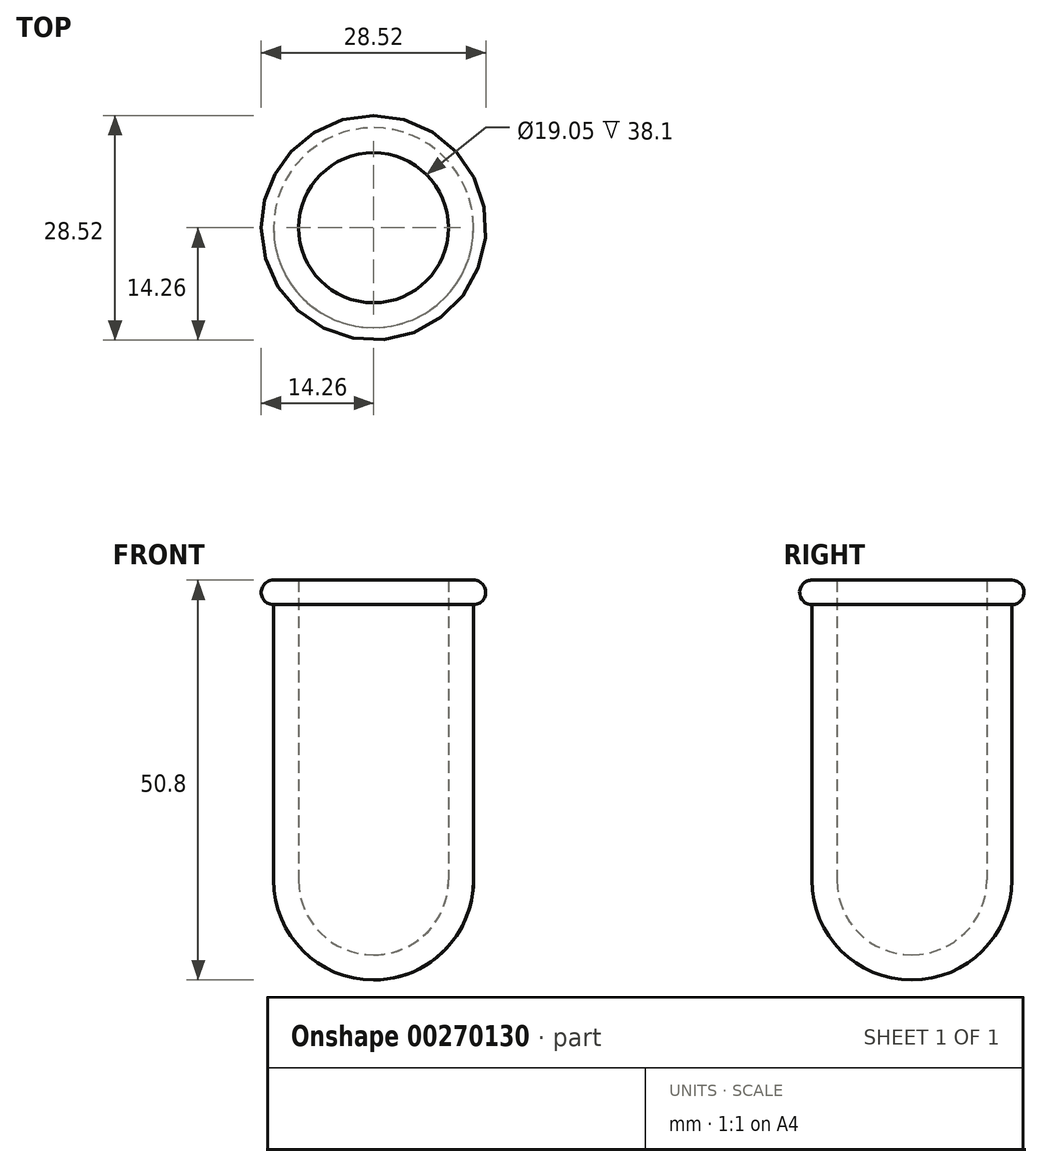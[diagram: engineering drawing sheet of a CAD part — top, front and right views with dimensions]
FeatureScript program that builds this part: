
annotation { "Feature Type Name" : "Feature", "Feature Type Description" : "" }
export const myFeature = defineFeature(function(context is Context, id is Id, definition is map)
    precondition{}
    {
        {
            var Q0;
            Q0=qCreatedBy(makeId("Front.planeOp"),FACE);
            var sketch = newSketch(context, id + "F0", { "sketchPlane" : qUnion([Q0])});
            skLineSegment(sketch, "E0", {"start": v(0, 0) * mm, "end": v(0, 50.8) * mm});
            skLineSegment(sketch, "E1", {"start": v(0, 50.8) * mm, "end": v(12.7, 50.8) * mm});
            skLineSegment(sketch, "E2", {"start": v(12.7, 50.8) * mm, "end": v(12.7, 0) * mm});
            skLineSegment(sketch, "E3", {"start": v(12.7, 0) * mm, "end": v(0, 0) * mm});
            skArc(sketch, "E4", {"start": v(12.7, 47.68) * mm, "mid": v(14.26, 49.24) * mm, "end": v(12.7, 50.8) * mm});
            skSolve(sketch);
        }
        {
            var Q0;
            Q0=makeQuery(id+"F0.imprint","IMPRINT",FACE,{"disambiguationData":[TD([[makeQuery(id+"F0.imprint","IMPRINT",EDGE,{"derivedFrom":sQuery(id+"F0.wireOp",EDGE,"E0")}),-1.0]])]});
            var Q1;
            {var subQ0=sQuery(id+"F0.wireOp",EDGE,"E4");Q1=makeQuery(id+"F0.imprint","IMPRINT",FACE,{"disambiguationData":[TD([[makeQuery(id+"F0.imprint","IMPRINT",EDGE,{"derivedFrom":subQ0}),1.0]])]});}
            var Q2;
            Q2=sQuery(id+"F0.wireOp",EDGE,"E0");
            revolve(context, id + "F1", {"entities" : qUnion([Q0, Q1]), "axis" : qUnion([Q2]), "revolveType" : RevolveType.FULL});
        }
        {
            var Q0;
            Q0=makeQuery(id+"F1.opRevolve","SWEPT_EDGE",EDGE,{"disambiguationData":[OSD([sQuery(id+"F0.wireOp",EDGE,"E2"),sQuery(id+"F0.wireOp",EDGE,"E3")])]});
            fillet(context, id + "F2", {"entities" : qUnion([Q0]), "radius" : 12.7 * mm, "tangentPropagation" : true, "allowEdgeOverflow" : false});
        }
        {
            var Q0;
            Q0=makeQuery(id+"F1.opRevolve","SWEPT_FACE",FACE,{"disambiguationData":[OSD([sQuery(id+"F0.wireOp",EDGE,"E1")])]});
            shell(context, id + "F3", {"entities" : qUnion([Q0]), "thickness" : 3.17 * mm});
        }
    });
